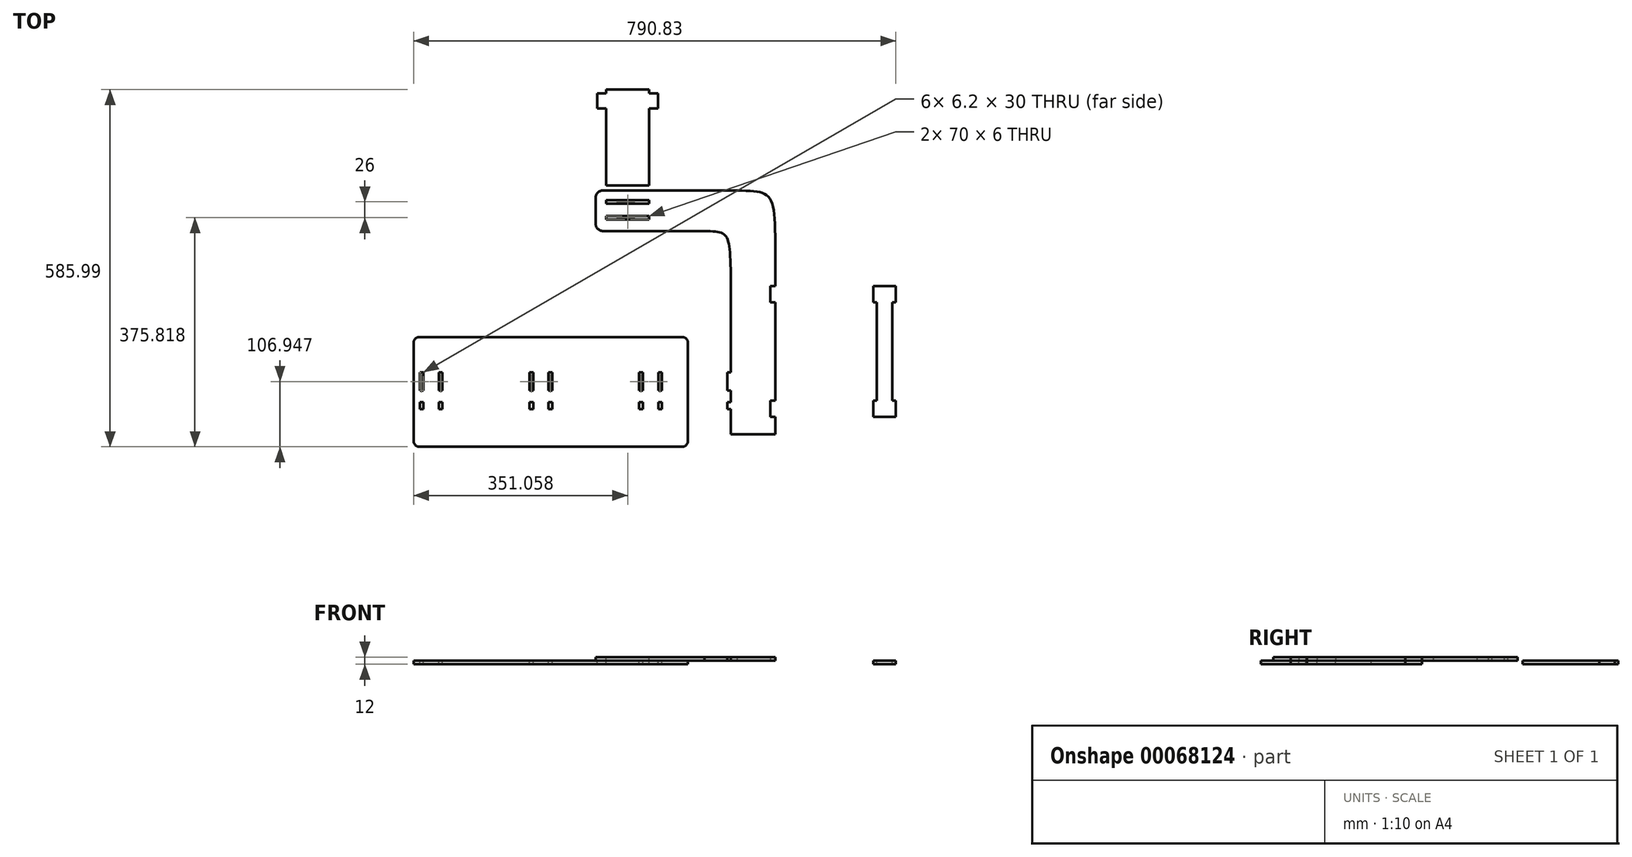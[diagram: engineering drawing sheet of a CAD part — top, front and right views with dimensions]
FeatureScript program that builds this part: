
annotation { "Feature Type Name" : "Feature", "Feature Type Description" : "" }
export const myFeature = defineFeature(function(context is Context, id is Id, definition is map)
    precondition{}
    {
        {
            var Q0;
            Q0=qCreatedBy(makeId("Top.planeOp"),FACE);
            var sketch = newSketch(context, id + "F0", { "sketchPlane" : qUnion([Q0])});
            skLineSegment(sketch, "E0.bottom", {"start": v(10, 0) * mm, "end": v(440, 0) * mm});
            skLineSegment(sketch, "E0.top", {"start": v(10, 180) * mm, "end": v(440, 180) * mm});
            skLineSegment(sketch, "E0.left", {"start": v(0, 10) * mm, "end": v(0, 170) * mm});
            skLineSegment(sketch, "E0.right", {"start": v(450, 10) * mm, "end": v(450, 170) * mm});
            skPoint(sketch, "E1.visualSharp", {"position": v(0, 180) * mm});
            skArc(sketch, "E1.filletArc", {"start": v(10, 180) * mm, "mid": v(2.93, 177.07) * mm, "end": v(0, 170) * mm});
            skPoint(sketch, "E2.visualSharp", {"position": v(450, 180) * mm});
            skArc(sketch, "E2.filletArc", {"start": v(450, 170) * mm, "mid": v(447.07, 177.07) * mm, "end": v(440, 180) * mm});
            skPoint(sketch, "E3.visualSharp", {"position": v(450, 0) * mm});
            skArc(sketch, "E3.filletArc", {"start": v(440, 0) * mm, "mid": v(447.07, 2.93) * mm, "end": v(450, 10) * mm});
            skPoint(sketch, "E4.visualSharp", {"position": v(0, 0) * mm});
            skArc(sketch, "E4.filletArc", {"start": v(0, 10) * mm, "mid": v(2.93, 2.93) * mm, "end": v(10, 0) * mm});
            skSolve(sketch);
        }
        {
            var Q0;
            Q0=makeQuery(id+"F0.imprint","IMPRINT",FACE,{"disambiguationData":[TD([[makeQuery(id+"F0.imprint","IMPRINT",EDGE,{"derivedFrom":sQuery(id+"F0.wireOp",EDGE,"E0.bottom")}),1.0]])]});
            extrude(context, id + "F1", {"entities" : qUnion([Q0]), "depth" : 6 * mm});
        }
        {
            var Q0;
            Q0=makeQuery(id+"F1.opExtrude","CAP_FACE",FACE,{"disambiguationData":[OSD([sQuery(id+"F0.wireOp",EDGE,"E0.bottom"),sQuery(id+"F0.wireOp",EDGE,"E0.top"),sQuery(id+"F0.wireOp",EDGE,"E0.left"),sQuery(id+"F0.wireOp",EDGE,"E0.right"),sQuery(id+"F0.wireOp",EDGE,"4207fe52-dffd-4da9-accc-93b81c2cf454"),sQuery(id+"F0.wireOp",EDGE,"789c2001-8988-4e37-93b7-ed076d86bb5b"),sQuery(id+"F0.wireOp",EDGE,"353d5666-f014-4095-a29d-f12433deb24c"),sQuery(id+"F0.wireOp",EDGE,"e61ba7d6-34ff-4ce0-8170-7ef8d0cdd7d2"),sQuery(id+"F0.wireOp",EDGE,"E1.filletArc"),sQuery(id+"F0.wireOp",EDGE,"E2.filletArc"),sQuery(id+"F0.wireOp",EDGE,"E3.filletArc"),sQuery(id+"F0.wireOp",EDGE,"E4.filletArc")])],"isStart":false});
            var sketch = newSketch(context, id + "F2", { "sketchPlane" : qUnion([Q0])});
            skLineSegment(sketch, "E5.bottom", {"start": v(10, 180) * mm, "end": v(440, 180) * mm, "construction": true});
            skLineSegment(sketch, "E5.top", {"start": v(10, 0) * mm, "end": v(440, 0) * mm, "construction": true});
            skLineSegment(sketch, "E5.left", {"start": v(10, 180) * mm, "end": v(10, 0) * mm, "construction": true});
            skLineSegment(sketch, "E5.right", {"start": v(440, 180) * mm, "end": v(440, 0) * mm, "construction": true});
            skLineSegment(sketch, "E6.bottom", {"start": v(0, 170) * mm, "end": v(450, 170) * mm, "construction": true});
            skLineSegment(sketch, "E6.top", {"start": v(0, 10) * mm, "end": v(450, 10) * mm, "construction": true});
            skLineSegment(sketch, "E6.left", {"start": v(0, 170) * mm, "end": v(0, 10) * mm, "construction": true});
            skLineSegment(sketch, "E6.right", {"start": v(450, 170) * mm, "end": v(450, 10) * mm, "construction": true});
            skLineSegment(sketch, "E7.bottom", {"start": v(16.2, 121.95) * mm, "end": v(10, 121.95) * mm});
            skLineSegment(sketch, "E7.top", {"start": v(16.2, 91.95) * mm, "end": v(10, 91.95) * mm});
            skLineSegment(sketch, "E7.left", {"start": v(16.2, 121.95) * mm, "end": v(16.2, 91.95) * mm});
            skLineSegment(sketch, "E7.right", {"start": v(10, 121.95) * mm, "end": v(10, 91.95) * mm});
            skLineSegment(sketch, "E8", {"start": v(16.2, 121.95) * mm, "end": v(153.1, 121.95) * mm, "construction": true});
            skLineSegment(sketch, "E9", {"start": v(10, 121.95) * mm, "end": v(0, 121.95) * mm, "construction": true});
            skLineSegment(sketch, "E10.bottom", {"start": v(10, 91.95) * mm, "end": v(16.2, 91.95) * mm, "construction": true});
            skLineSegment(sketch, "E10.top", {"start": v(10, 73.47) * mm, "end": v(16.2, 73.47) * mm, "construction": true});
            skLineSegment(sketch, "E10.left", {"start": v(10, 91.95) * mm, "end": v(10, 73.47) * mm, "construction": true});
            skLineSegment(sketch, "E10.right", {"start": v(16.2, 91.95) * mm, "end": v(16.2, 73.47) * mm, "construction": true});
            skLineSegment(sketch, "E11.bottom", {"start": v(10, 73.47) * mm, "end": v(16.2, 73.47) * mm});
            skLineSegment(sketch, "E11.top", {"start": v(10, 61.95) * mm, "end": v(16.2, 61.95) * mm});
            skLineSegment(sketch, "E11.left", {"start": v(10, 61.95) * mm, "end": v(10, 73.47) * mm});
            skLineSegment(sketch, "E11.right", {"start": v(16.2, 61.95) * mm, "end": v(16.2, 73.47) * mm});
            skLineSegment(sketch, "E12.bottom", {"start": v(41.2, 73.47) * mm, "end": v(47.4, 73.47) * mm});
            skLineSegment(sketch, "E12.top", {"start": v(41.2, 61.95) * mm, "end": v(47.4, 61.95) * mm});
            skLineSegment(sketch, "E12.left", {"start": v(41.2, 61.95) * mm, "end": v(41.2, 73.47) * mm});
            skLineSegment(sketch, "E12.right", {"start": v(47.4, 61.95) * mm, "end": v(47.4, 73.47) * mm});
            skLineSegment(sketch, "E13.bottom", {"start": v(41.2, 91.95) * mm, "end": v(47.4, 91.95) * mm});
            skLineSegment(sketch, "E13.top", {"start": v(41.2, 121.95) * mm, "end": v(47.4, 121.95) * mm});
            skLineSegment(sketch, "E13.left", {"start": v(41.2, 91.95) * mm, "end": v(41.2, 121.95) * mm});
            skLineSegment(sketch, "E13.right", {"start": v(47.4, 91.95) * mm, "end": v(47.4, 121.95) * mm});
            skLineSegment(sketch, "E14.1.0.0", {"start": v(227.4, 91.95) * mm, "end": v(227.4, 121.95) * mm});
            skLineSegment(sketch, "E14.1.0.1", {"start": v(190, 121.95) * mm, "end": v(190, 91.95) * mm});
            skLineSegment(sketch, "E14.1.0.2", {"start": v(196.2, 91.95) * mm, "end": v(196.2, 73.47) * mm, "construction": true});
            skLineSegment(sketch, "E14.1.0.3", {"start": v(221.2, 91.95) * mm, "end": v(221.2, 121.95) * mm});
            skLineSegment(sketch, "E14.1.0.4", {"start": v(196.2, 121.95) * mm, "end": v(196.2, 91.95) * mm});
            skLineSegment(sketch, "E14.1.0.5", {"start": v(190, 91.95) * mm, "end": v(190, 73.47) * mm, "construction": true});
            skLineSegment(sketch, "E14.1.0.6", {"start": v(190, 61.95) * mm, "end": v(196.2, 61.95) * mm});
            skLineSegment(sketch, "E14.1.0.7", {"start": v(221.2, 73.47) * mm, "end": v(227.4, 73.47) * mm});
            skLineSegment(sketch, "E14.1.0.8", {"start": v(221.2, 61.95) * mm, "end": v(227.4, 61.95) * mm});
            skLineSegment(sketch, "E14.1.0.9", {"start": v(227.4, 61.95) * mm, "end": v(227.4, 73.47) * mm});
            skLineSegment(sketch, "E14.1.0.10", {"start": v(196.2, 61.95) * mm, "end": v(196.2, 73.47) * mm});
            skLineSegment(sketch, "E14.1.0.11", {"start": v(221.2, 91.95) * mm, "end": v(227.4, 91.95) * mm});
            skLineSegment(sketch, "E14.1.0.12", {"start": v(221.2, 121.95) * mm, "end": v(227.4, 121.95) * mm});
            skLineSegment(sketch, "E14.1.0.13", {"start": v(221.2, 61.95) * mm, "end": v(221.2, 73.47) * mm});
            skLineSegment(sketch, "E14.1.0.14", {"start": v(190, 61.95) * mm, "end": v(190, 73.47) * mm});
            skLineSegment(sketch, "E14.1.0.15", {"start": v(196.2, 121.95) * mm, "end": v(190, 121.95) * mm});
            skLineSegment(sketch, "E14.1.0.16", {"start": v(190, 73.47) * mm, "end": v(196.2, 73.47) * mm});
            skLineSegment(sketch, "E14.1.0.17", {"start": v(196.2, 91.95) * mm, "end": v(190, 91.95) * mm});
            skLineSegment(sketch, "E14.1.0.18", {"start": v(190, 91.95) * mm, "end": v(196.2, 91.95) * mm, "construction": true});
            skLineSegment(sketch, "E14.1.0.19", {"start": v(190, 73.47) * mm, "end": v(196.2, 73.47) * mm, "construction": true});
            skLineSegment(sketch, "E14.2.0.0", {"start": v(407.4, 91.95) * mm, "end": v(407.4, 121.95) * mm});
            skLineSegment(sketch, "E14.2.0.1", {"start": v(370, 121.95) * mm, "end": v(370, 91.95) * mm});
            skLineSegment(sketch, "E14.2.0.2", {"start": v(376.2, 91.95) * mm, "end": v(376.2, 73.47) * mm, "construction": true});
            skLineSegment(sketch, "E14.2.0.3", {"start": v(401.2, 91.95) * mm, "end": v(401.2, 121.95) * mm});
            skLineSegment(sketch, "E14.2.0.4", {"start": v(376.2, 121.95) * mm, "end": v(376.2, 91.95) * mm});
            skLineSegment(sketch, "E14.2.0.5", {"start": v(370, 91.95) * mm, "end": v(370, 73.47) * mm, "construction": true});
            skLineSegment(sketch, "E14.2.0.6", {"start": v(370, 61.95) * mm, "end": v(376.2, 61.95) * mm});
            skLineSegment(sketch, "E14.2.0.7", {"start": v(401.2, 73.47) * mm, "end": v(407.4, 73.47) * mm});
            skLineSegment(sketch, "E14.2.0.8", {"start": v(401.2, 61.95) * mm, "end": v(407.4, 61.95) * mm});
            skLineSegment(sketch, "E14.2.0.9", {"start": v(407.4, 61.95) * mm, "end": v(407.4, 73.47) * mm});
            skLineSegment(sketch, "E14.2.0.10", {"start": v(376.2, 61.95) * mm, "end": v(376.2, 73.47) * mm});
            skLineSegment(sketch, "E14.2.0.11", {"start": v(401.2, 91.95) * mm, "end": v(407.4, 91.95) * mm});
            skLineSegment(sketch, "E14.2.0.12", {"start": v(401.2, 121.95) * mm, "end": v(407.4, 121.95) * mm});
            skLineSegment(sketch, "E14.2.0.13", {"start": v(401.2, 61.95) * mm, "end": v(401.2, 73.47) * mm});
            skLineSegment(sketch, "E14.2.0.14", {"start": v(370, 61.95) * mm, "end": v(370, 73.47) * mm});
            skLineSegment(sketch, "E14.2.0.15", {"start": v(376.2, 121.95) * mm, "end": v(370, 121.95) * mm});
            skLineSegment(sketch, "E14.2.0.16", {"start": v(370, 73.47) * mm, "end": v(376.2, 73.47) * mm});
            skLineSegment(sketch, "E14.2.0.17", {"start": v(376.2, 91.95) * mm, "end": v(370, 91.95) * mm});
            skLineSegment(sketch, "E14.2.0.18", {"start": v(370, 91.95) * mm, "end": v(376.2, 91.95) * mm, "construction": true});
            skLineSegment(sketch, "E14.2.0.19", {"start": v(370, 73.47) * mm, "end": v(376.2, 73.47) * mm, "construction": true});
            skLineSegment(sketch, "E14.direction1", {"start": v(47.4, 91.95) * mm, "end": v(227.4, 91.95) * mm, "construction": true});
            skSolve(sketch);
        }
        {
            var Q0;
            Q0 = qSketchRegion(id + "F2", true);
            extrude(context, id + "F3", {"entities" : qUnion([Q0]), "operationType" : NewBodyOperationType.REMOVE, "oppositeDirection" : true, "depth" : 25 * mm});
        }
        {
            var Q0;
            Q0=makeQuery(id+"F1.opExtrude","CAP_FACE",FACE,{"disambiguationData":[OSD([sQuery(id+"F0.wireOp",EDGE,"E0.bottom"),sQuery(id+"F0.wireOp",EDGE,"E0.top"),sQuery(id+"F0.wireOp",EDGE,"E0.left"),sQuery(id+"F0.wireOp",EDGE,"E0.right"),sQuery(id+"F0.wireOp",EDGE,"4207fe52-dffd-4da9-accc-93b81c2cf454"),sQuery(id+"F0.wireOp",EDGE,"789c2001-8988-4e37-93b7-ed076d86bb5b"),sQuery(id+"F0.wireOp",EDGE,"353d5666-f014-4095-a29d-f12433deb24c"),sQuery(id+"F0.wireOp",EDGE,"e61ba7d6-34ff-4ce0-8170-7ef8d0cdd7d2"),sQuery(id+"F0.wireOp",EDGE,"E1.filletArc"),sQuery(id+"F0.wireOp",EDGE,"E2.filletArc"),sQuery(id+"F0.wireOp",EDGE,"E3.filletArc"),sQuery(id+"F0.wireOp",EDGE,"E4.filletArc")])],"isStart":false});
            var sketch = newSketch(context, id + "F4", { "sketchPlane" : qUnion([Q0])});
            skLineSegment(sketch, "E15.bottom", {"start": v(407.4, 121.95) * mm, "end": v(514.32, 121.95) * mm, "construction": true});
            skLineSegment(sketch, "E15.top", {"start": v(407.4, 73.47) * mm, "end": v(514.69, 73.47) * mm, "construction": true});
            skLineSegment(sketch, "E15.left", {"start": v(407.4, 121.95) * mm, "end": v(407.4, 73.47) * mm, "construction": true});
            skLineSegment(sketch, "E16.bottom", {"start": v(407.4, 91.95) * mm, "end": v(514.69, 91.95) * mm, "construction": true});
            skLineSegment(sketch, "E16.top", {"start": v(407.4, 61.95) * mm, "end": v(514.69, 61.95) * mm, "construction": true});
            skLineSegment(sketch, "E16.left", {"start": v(407.4, 91.95) * mm, "end": v(407.4, 61.95) * mm, "construction": true});
            skLineSegment(sketch, "E17.bottom", {"start": v(514.32, 121.95) * mm, "end": v(520.32, 121.95) * mm});
            skLineSegment(sketch, "E17.top", {"start": v(514.32, 91.95) * mm, "end": v(520.32, 91.95) * mm});
            skLineSegment(sketch, "E17.left", {"start": v(514.32, 121.95) * mm, "end": v(514.32, 91.95) * mm});
            skLineSegment(sketch, "E18.bottom", {"start": v(514.69, 61.95) * mm, "end": v(520.32, 61.95) * mm});
            skLineSegment(sketch, "E18.top", {"start": v(514.69, 73.47) * mm, "end": v(520.32, 73.47) * mm});
            skLineSegment(sketch, "E18.left", {"start": v(514.69, 73.47) * mm, "end": v(514.69, 61.95) * mm});
            skLineSegment(sketch, "E19.bottom", {"start": v(520.32, 20.24) * mm, "end": v(593.2, 20.24) * mm});
            skLineSegment(sketch, "E19.left", {"start": v(520.32, 20.24) * mm, "end": v(520.32, 61.95) * mm});
            skLineSegment(sketch, "E19.right", {"start": v(593.2, 20.24) * mm, "end": v(593.2, 307.47) * mm});
            skLineSegment(sketch, "E20", {"start": v(310.4, 354.03) * mm, "end": v(476.9, 354.03) * mm});
            skLineSegment(sketch, "E21", {"start": v(298.4, 408.45) * mm, "end": v(298.4, 366.03) * mm});
            skLineSegment(sketch, "E22", {"start": v(530.11, 420.45) * mm, "end": v(310.4, 420.45) * mm});
            skLineSegment(sketch, "E23.trimOffspring", {"start": v(520.32, 121.95) * mm, "end": v(520.32, 282.1) * mm});
            skLineSegment(sketch, "E24.trimOffspring", {"start": v(520.32, 73.47) * mm, "end": v(520.32, 91.95) * mm});
            skPoint(sketch, "E25.visualSharp", {"position": v(298.4, 420.45) * mm});
            skArc(sketch, "E25.filletArc", {"start": v(310.4, 420.45) * mm, "mid": v(301.92, 416.93) * mm, "end": v(298.4, 408.45) * mm});
            skPoint(sketch, "E26.visualSharp", {"position": v(298.4, 354.03) * mm});
            skArc(sketch, "E26.filletArc", {"start": v(298.4, 366.03) * mm, "mid": v(301.92, 357.54) * mm, "end": v(310.4, 354.03) * mm});
            skFitSpline(sketch, "E27", {"points": [v(476.9, 354.03) * mm, v(520.32, 282.1) * mm], "startDerivative": vector(123.18, -4.2) * mm, "endDerivative": vector(7.08, -211.58) * mm});
            skFitSpline(sketch, "E28", {"points": [v(530.11, 420.45) * mm, v(593.2, 307.47) * mm], "startDerivative": vector(189.29, -3.4) * mm, "endDerivative": vector(0, -335.53) * mm});
            skSolve(sketch);
        }
        {
            var Q0;
            Q0 = qSketchRegion(id + "F4", true);
            extrude(context, id + "F5", {"entities" : qUnion([Q0]), "depth" : 6 * mm});
        }
        {
            var Q0;
            Q0=makeQuery(id+"F5.opExtrude","CAP_FACE",FACE,{"disambiguationData":[OSD([sQuery(id+"F4.wireOp",EDGE,"E17.bottom"),sQuery(id+"F4.wireOp",EDGE,"E17.top"),sQuery(id+"F4.wireOp",EDGE,"E17.left"),sQuery(id+"F4.wireOp",EDGE,"E18.bottom"),sQuery(id+"F4.wireOp",EDGE,"E18.top"),sQuery(id+"F4.wireOp",EDGE,"E18.left"),sQuery(id+"F4.wireOp",EDGE,"E19.bottom"),sQuery(id+"F4.wireOp",EDGE,"E19.left"),sQuery(id+"F4.wireOp",EDGE,"E19.right"),sQuery(id+"F4.wireOp",EDGE,"tWsiTS39-3US8-nB4P-Z9d9-HeoiJeJ519z0"),sQuery(id+"F4.wireOp",EDGE,"E20"),sQuery(id+"F4.wireOp",EDGE,"E21"),sQuery(id+"F4.wireOp",EDGE,"E22"),sQuery(id+"F4.wireOp",EDGE,"gugv8Hga-iz7I-GJb2-wqf6-1LZM5Z3AYTYz"),sQuery(id+"F4.wireOp",EDGE,"E23.trimOffspring"),sQuery(id+"F4.wireOp",EDGE,"E24.trimOffspring")])],"isStart":false});
            var sketch = newSketch(context, id + "F6", { "sketchPlane" : qUnion([Q0])});
            skLineSegment(sketch, "E29.bottom", {"start": v(316.06, 398.82) * mm, "end": v(386.06, 398.82) * mm});
            skLineSegment(sketch, "E29.top", {"start": v(316.06, 404.82) * mm, "end": v(386.06, 404.82) * mm});
            skLineSegment(sketch, "E29.left", {"start": v(316.06, 404.82) * mm, "end": v(316.06, 398.82) * mm});
            skLineSegment(sketch, "E29.right", {"start": v(386.06, 404.82) * mm, "end": v(386.06, 398.82) * mm});
            skLineSegment(sketch, "E30.bottom", {"start": v(316.06, 378.82) * mm, "end": v(386.06, 378.82) * mm});
            skLineSegment(sketch, "E30.top", {"start": v(316.06, 372.82) * mm, "end": v(386.06, 372.82) * mm});
            skLineSegment(sketch, "E30.left", {"start": v(316.06, 378.82) * mm, "end": v(316.06, 372.82) * mm});
            skLineSegment(sketch, "E30.right", {"start": v(386.06, 378.82) * mm, "end": v(386.06, 372.82) * mm});
            skSolve(sketch);
        }
        {
            var Q0;
            Q0 = qSketchRegion(id + "F6", true);
            extrude(context, id + "F7", {"entities" : qUnion([Q0]), "operationType" : NewBodyOperationType.REMOVE, "oppositeDirection" : true, "depth" : 25 * mm});
        }
        {
            var Q0;
            Q0=makeQuery(id+"F5.opExtrude","CAP_FACE",FACE,{"disambiguationData":[OSD([sQuery(id+"F4.wireOp",EDGE,"E17.bottom"),sQuery(id+"F4.wireOp",EDGE,"E17.top"),sQuery(id+"F4.wireOp",EDGE,"E17.left"),sQuery(id+"F4.wireOp",EDGE,"E18.bottom"),sQuery(id+"F4.wireOp",EDGE,"E18.top"),sQuery(id+"F4.wireOp",EDGE,"E18.left"),sQuery(id+"F4.wireOp",EDGE,"E19.bottom"),sQuery(id+"F4.wireOp",EDGE,"E19.left"),sQuery(id+"F4.wireOp",EDGE,"E19.right"),sQuery(id+"F4.wireOp",EDGE,"E20"),sQuery(id+"F4.wireOp",EDGE,"E21"),sQuery(id+"F4.wireOp",EDGE,"E22"),sQuery(id+"F4.wireOp",EDGE,"E23.trimOffspring"),sQuery(id+"F4.wireOp",EDGE,"E24.trimOffspring"),sQuery(id+"F4.wireOp",EDGE,"E25.filletArc"),sQuery(id+"F4.wireOp",EDGE,"E26.filletArc"),sQuery(id+"F4.wireOp",EDGE,"E27"),sQuery(id+"F4.wireOp",EDGE,"E28")])],"isStart":true});
            var sketch = newSketch(context, id + "F8", { "sketchPlane" : qUnion([Q0])});
            skLineSegment(sketch, "E31.bottom", {"start": v(593.2, -48.77) * mm, "end": v(584.75, -48.77) * mm});
            skLineSegment(sketch, "E31.top", {"start": v(593.2, -75.52) * mm, "end": v(584.75, -75.52) * mm});
            skLineSegment(sketch, "E31.left", {"start": v(593.2, -48.77) * mm, "end": v(593.2, -75.52) * mm});
            skLineSegment(sketch, "E31.right", {"start": v(584.75, -48.77) * mm, "end": v(584.75, -75.52) * mm});
            skPoint(sketch, "E32.oppositeSnap0", {"position": v(584.75, -62.14) * mm});
            skLineSegment(sketch, "E32.bottom", {"start": v(593.2, -263.6) * mm, "end": v(584.75, -263.6) * mm});
            skLineSegment(sketch, "E32.top", {"start": v(593.2, -236.86) * mm, "end": v(584.75, -236.86) * mm});
            skLineSegment(sketch, "E32.left", {"start": v(593.2, -263.6) * mm, "end": v(593.2, -236.86) * mm});
            skLineSegment(sketch, "E32.right", {"start": v(584.75, -263.6) * mm, "end": v(584.75, -236.86) * mm});
            skSolve(sketch);
        }
        {
            var Q0;
            Q0=makeQuery(id+"F8.imprint","IMPRINT",FACE,{"disambiguationData":[TD([[makeQuery(id+"F8.imprint","IMPRINT",EDGE,{"derivedFrom":sQuery(id+"F8.wireOp",EDGE,"E32.bottom")}),-1.0]])]});
            var Q1;
            Q1=makeQuery(id+"F8.imprint","IMPRINT",FACE,{"disambiguationData":[TD([[makeQuery(id+"F8.imprint","IMPRINT",EDGE,{"derivedFrom":sQuery(id+"F8.wireOp",EDGE,"E31.bottom")}),1.0]])]});
            extrude(context, id + "F9", {"entities" : qUnion([Q0, Q1]), "operationType" : NewBodyOperationType.REMOVE, "oppositeDirection" : true, "depth" : 25 * mm});
        }
        {
            var Q0;
            Q0=makeQuery(id+"F5.opExtrude","CAP_FACE",FACE,{"disambiguationData":[OSD([sQuery(id+"F4.wireOp",EDGE,"E17.bottom"),sQuery(id+"F4.wireOp",EDGE,"E17.top"),sQuery(id+"F4.wireOp",EDGE,"E17.left"),sQuery(id+"F4.wireOp",EDGE,"E18.bottom"),sQuery(id+"F4.wireOp",EDGE,"E18.top"),sQuery(id+"F4.wireOp",EDGE,"E18.left"),sQuery(id+"F4.wireOp",EDGE,"E19.bottom"),sQuery(id+"F4.wireOp",EDGE,"E19.left"),sQuery(id+"F4.wireOp",EDGE,"E19.right"),sQuery(id+"F4.wireOp",EDGE,"E20"),sQuery(id+"F4.wireOp",EDGE,"E21"),sQuery(id+"F4.wireOp",EDGE,"E22"),sQuery(id+"F4.wireOp",EDGE,"E23.trimOffspring"),sQuery(id+"F4.wireOp",EDGE,"E24.trimOffspring"),sQuery(id+"F4.wireOp",EDGE,"E25.filletArc"),sQuery(id+"F4.wireOp",EDGE,"E26.filletArc"),sQuery(id+"F4.wireOp",EDGE,"E27"),sQuery(id+"F4.wireOp",EDGE,"E28")])],"isStart":true});
            var sketch = newSketch(context, id + "F10", { "sketchPlane" : qUnion([Q0])});
            skLineSegment(sketch, "E33.bottom", {"start": v(593.2, -263.6) * mm, "end": v(784.83, -263.6) * mm, "construction": true});
            skLineSegment(sketch, "E33.top", {"start": v(593.2, -48.77) * mm, "end": v(784.83, -48.77) * mm, "construction": true});
            skLineSegment(sketch, "E33.left", {"start": v(593.2, -263.6) * mm, "end": v(593.2, -48.77) * mm, "construction": true});
            skLineSegment(sketch, "E33.right", {"start": v(784.83, -263.6) * mm, "end": v(784.83, -48.77) * mm, "construction": true});
            skLineSegment(sketch, "E34.bottom", {"start": v(593.2, -236.86) * mm, "end": v(759.83, -236.86) * mm, "construction": true});
            skLineSegment(sketch, "E34.top", {"start": v(593.2, -75.52) * mm, "end": v(759.83, -75.52) * mm, "construction": true});
            skLineSegment(sketch, "E34.left", {"start": v(593.2, -236.86) * mm, "end": v(593.2, -75.52) * mm, "construction": true});
            skLineSegment(sketch, "E34.right", {"start": v(759.83, -236.86) * mm, "end": v(759.83, -75.52) * mm, "construction": true});
            skLineSegment(sketch, "E35.bottom", {"start": v(759.83, -263.6) * mm, "end": v(784.83, -263.6) * mm});
            skLineSegment(sketch, "E35.top", {"start": v(759.83, -48.77) * mm, "end": v(784.83, -48.77) * mm});
            skLineSegment(sketch, "E35.left", {"start": v(759.83, -236.86) * mm, "end": v(759.83, -75.52) * mm});
            skLineSegment(sketch, "E35.right", {"start": v(784.83, -236.86) * mm, "end": v(784.83, -75.52) * mm});
            skLineSegment(sketch, "E36.bottom", {"start": v(759.83, -263.6) * mm, "end": v(753.83, -263.6) * mm});
            skLineSegment(sketch, "E36.top", {"start": v(759.83, -236.86) * mm, "end": v(753.83, -236.86) * mm});
            skLineSegment(sketch, "E36.right", {"start": v(753.83, -263.6) * mm, "end": v(753.83, -236.86) * mm});
            skLineSegment(sketch, "E37.bottom", {"start": v(759.83, -48.77) * mm, "end": v(753.83, -48.77) * mm});
            skLineSegment(sketch, "E37.top", {"start": v(759.83, -75.52) * mm, "end": v(753.83, -75.52) * mm});
            skLineSegment(sketch, "E37.right", {"start": v(753.83, -48.77) * mm, "end": v(753.83, -75.52) * mm});
            skLineSegment(sketch, "E38.bottom", {"start": v(784.83, -263.6) * mm, "end": v(790.83, -263.6) * mm});
            skLineSegment(sketch, "E38.top", {"start": v(784.83, -236.86) * mm, "end": v(790.83, -236.86) * mm});
            skLineSegment(sketch, "E38.right", {"start": v(790.83, -263.6) * mm, "end": v(790.83, -236.86) * mm});
            skLineSegment(sketch, "E39.bottom", {"start": v(784.83, -48.77) * mm, "end": v(790.83, -48.77) * mm});
            skLineSegment(sketch, "E39.top", {"start": v(784.83, -75.52) * mm, "end": v(790.83, -75.52) * mm});
            skLineSegment(sketch, "E39.right", {"start": v(790.83, -48.77) * mm, "end": v(790.83, -75.52) * mm});
            skSolve(sketch);
        }
        {
            var Q0;
            Q0=makeQuery(id+"F10.imprint","IMPRINT",FACE,{"disambiguationData":[TD([[makeQuery(id+"F10.imprint","IMPRINT",EDGE,{"derivedFrom":sQuery(id+"F10.wireOp",EDGE,"E35.bottom")}),1.0]])]});
            extrude(context, id + "F11", {"entities" : qUnion([Q0]), "depth" : 6 * mm});
        }
        {
            var Q0;
            Q0=makeQuery(id+"F5.opExtrude","CAP_FACE",FACE,{"disambiguationData":[OSD([sQuery(id+"F4.wireOp",EDGE,"E17.bottom"),sQuery(id+"F4.wireOp",EDGE,"E17.top"),sQuery(id+"F4.wireOp",EDGE,"E17.left"),sQuery(id+"F4.wireOp",EDGE,"E18.bottom"),sQuery(id+"F4.wireOp",EDGE,"E18.top"),sQuery(id+"F4.wireOp",EDGE,"E18.left"),sQuery(id+"F4.wireOp",EDGE,"E19.bottom"),sQuery(id+"F4.wireOp",EDGE,"E19.left"),sQuery(id+"F4.wireOp",EDGE,"E19.right"),sQuery(id+"F4.wireOp",EDGE,"E20"),sQuery(id+"F4.wireOp",EDGE,"E21"),sQuery(id+"F4.wireOp",EDGE,"E22"),sQuery(id+"F4.wireOp",EDGE,"E23.trimOffspring"),sQuery(id+"F4.wireOp",EDGE,"E24.trimOffspring"),sQuery(id+"F4.wireOp",EDGE,"E25.filletArc"),sQuery(id+"F4.wireOp",EDGE,"E26.filletArc"),sQuery(id+"F4.wireOp",EDGE,"E27"),sQuery(id+"F4.wireOp",EDGE,"E28")])],"isStart":true});
            var sketch = newSketch(context, id + "F12", { "sketchPlane" : qUnion([Q0])});
            skLineSegment(sketch, "E40.bottom", {"start": v(386.06, -404.82) * mm, "end": v(316.06, -404.82) * mm, "construction": true});
            skLineSegment(sketch, "E40.top", {"start": v(386.06, -549) * mm, "end": v(316.06, -549) * mm, "construction": true});
            skLineSegment(sketch, "E40.left", {"start": v(386.06, -404.82) * mm, "end": v(386.06, -549) * mm, "construction": true});
            skLineSegment(sketch, "E40.right", {"start": v(316.06, -404.82) * mm, "end": v(316.06, -549) * mm, "construction": true});
            skLineSegment(sketch, "E41.bottom", {"start": v(386.06, -549) * mm, "end": v(316.06, -549) * mm});
            skLineSegment(sketch, "E41.top", {"start": v(386.06, -555) * mm, "end": v(316.06, -555) * mm});
            skLineSegment(sketch, "E41.left", {"start": v(386.06, -549) * mm, "end": v(386.06, -555) * mm});
            skLineSegment(sketch, "E41.right", {"start": v(316.06, -549) * mm, "end": v(316.06, -555) * mm});
            skLineSegment(sketch, "E42.bottom", {"start": v(401.06, -555) * mm, "end": v(301.06, -555) * mm});
            skLineSegment(sketch, "E42.top", {"start": v(401.06, -580) * mm, "end": v(301.06, -580) * mm});
            skLineSegment(sketch, "E42.left", {"start": v(401.06, -555) * mm, "end": v(401.06, -580) * mm});
            skLineSegment(sketch, "E42.right", {"start": v(301.06, -555) * mm, "end": v(301.06, -580) * mm});
            skLineSegment(sketch, "E43.bottom", {"start": v(316.06, -580) * mm, "end": v(386.06, -580) * mm});
            skLineSegment(sketch, "E43.top", {"start": v(316.06, -586) * mm, "end": v(386.06, -586) * mm});
            skLineSegment(sketch, "E43.left", {"start": v(316.06, -580) * mm, "end": v(316.06, -586) * mm});
            skLineSegment(sketch, "E43.right", {"start": v(386.06, -580) * mm, "end": v(386.06, -586) * mm});
            skLineSegment(sketch, "E44", {"start": v(401.06, -580) * mm, "end": v(301.06, -555) * mm, "construction": true});
            skLineSegment(sketch, "E45", {"start": v(386.06, -586) * mm, "end": v(316.06, -580) * mm, "construction": true});
            skLineSegment(sketch, "E46", {"start": v(386.06, -555) * mm, "end": v(316.06, -549) * mm, "construction": true});
            skPoint(sketch, "E47", {"position": v(351.06, -567.5) * mm});
            skPoint(sketch, "E48", {"position": v(351.06, -583) * mm});
            skPoint(sketch, "E49", {"position": v(351.06, -552) * mm});
            skLineSegment(sketch, "E50", {"start": v(351.06, -583) * mm, "end": v(351.06, -567.5) * mm, "construction": true});
            skLineSegment(sketch, "E51", {"start": v(351.06, -552) * mm, "end": v(351.06, -567.5) * mm, "construction": true});
            skLineSegment(sketch, "E52.top", {"start": v(386.06, -539) * mm, "end": v(316.06, -539) * mm});
            skLineSegment(sketch, "E52.left", {"start": v(386.06, -549) * mm, "end": v(386.06, -539) * mm});
            skLineSegment(sketch, "E52.right", {"start": v(316.06, -549) * mm, "end": v(316.06, -539) * mm});
            skLineSegment(sketch, "E53.top", {"start": v(386.06, -429) * mm, "end": v(316.06, -429) * mm});
            skLineSegment(sketch, "E53.left", {"start": v(386.06, -539) * mm, "end": v(386.06, -429) * mm});
            skLineSegment(sketch, "E53.right", {"start": v(316.06, -539) * mm, "end": v(316.06, -429) * mm});
            skSolve(sketch);
        }
        {
            var Q0;
            Q0 = qSketchRegion(id + "F12", true);
            extrude(context, id + "F13", {"entities" : qUnion([Q0]), "depth" : 6 * mm});
        }
    });
